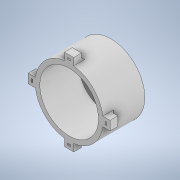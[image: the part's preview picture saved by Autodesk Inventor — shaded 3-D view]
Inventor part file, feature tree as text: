
AUTODESK INVENTOR PART (.ipt)
format: ipt  version: 2020 (Build 240168000, 168)  size: 359,936 bytes
history: native  units: mm
features: extrude x3, sketch x3, other x1, chamfer x1, pattern_circular x1
ambient origin geometry x8: Origin, YZ Plane, XZ Plane, XY Plane, X Axis, Y Axis, Z Axis, Center Point
bodies: Body1 (feature_tree)
feature tree (9):
  other  "솔리드1"
  extrude  "돌출1"  Depth=44.0mm
  extrude  "돌출2"  Depth=2.0mm TaperAngle=0.0deg
  extrude  "돌출3"  Depth=25.0mm TaperAngle=0.0deg
  chamfer  "모따기1"  Distance=38.0mm
  pattern_circular  "원형 패턴1"  [2 undecoded]
  sketch  "스케치1"
  sketch  "스케치2"
  sketch  "스케치3"
note: 2 required parameter values undecoded (feature->parameter linkage not recoverable at this tier; creation-order binding heuristic only, values carry confidence <= 0.55)
